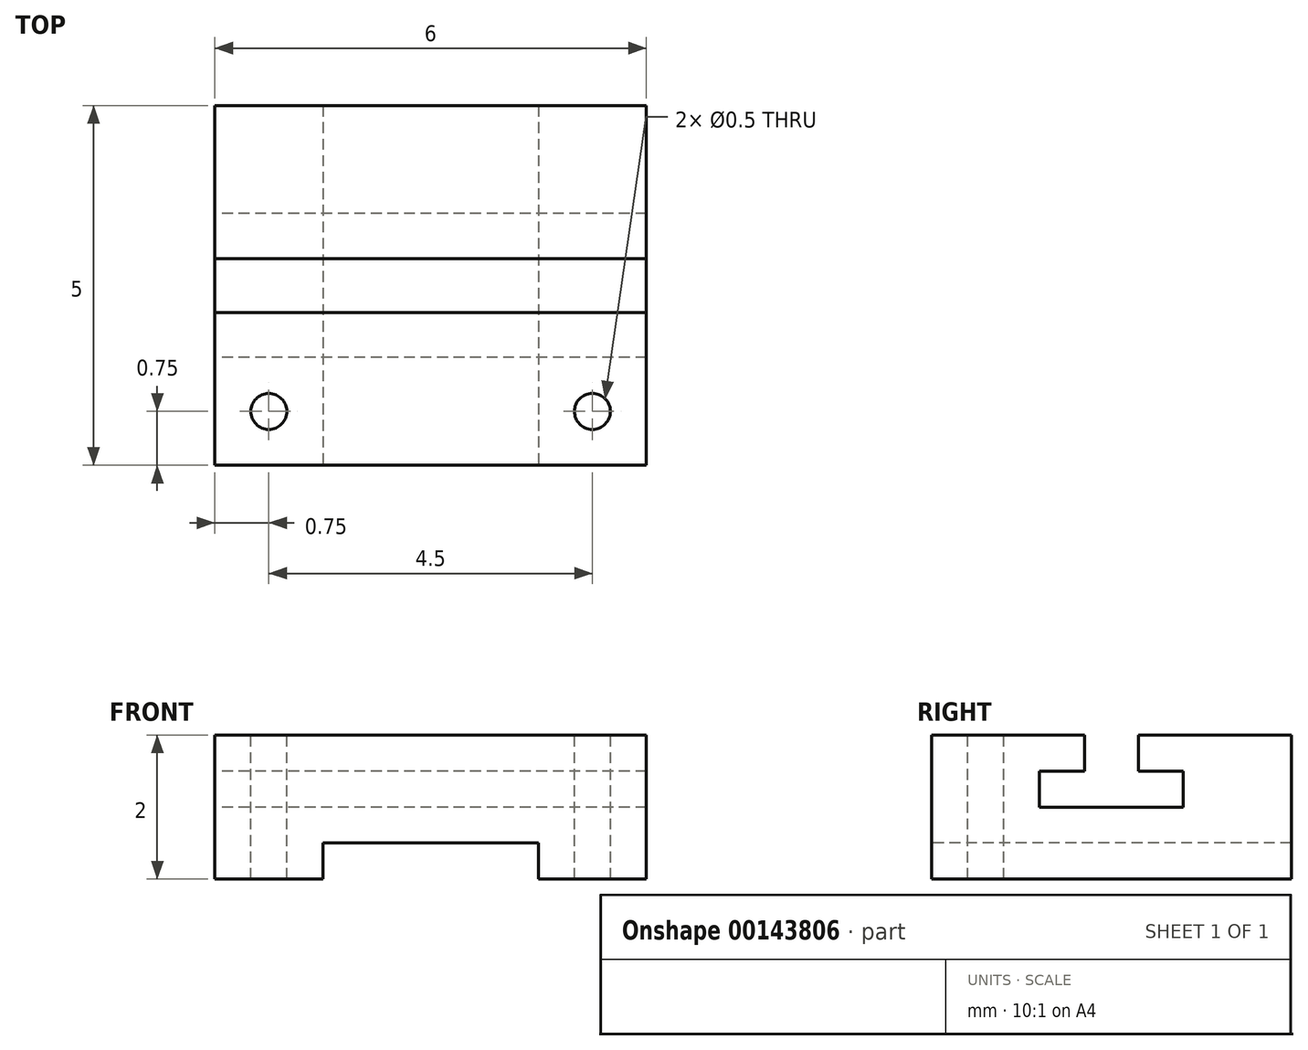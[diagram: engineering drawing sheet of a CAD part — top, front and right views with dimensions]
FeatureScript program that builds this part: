
annotation { "Feature Type Name" : "Feature", "Feature Type Description" : "" }
export const myFeature = defineFeature(function(context is Context, id is Id, definition is map)
    precondition{}
    {
        {
            var Q0;
            Q0=qCreatedBy(makeId("Right.planeOp"),FACE);
            var sketch = newSketch(context, id + "F0", { "sketchPlane" : qUnion([Q0])});
            skLineSegment(sketch, "E0", {"start": v(0, 0) * mm, "end": v(0, 2) * mm});
            skLineSegment(sketch, "E1", {"start": v(0, 2) * mm, "end": v(2.12, 2) * mm});
            skLineSegment(sketch, "E2", {"start": v(2.12, 2) * mm, "end": v(2.12, 1.5) * mm});
            skLineSegment(sketch, "E3", {"start": v(2.12, 1.5) * mm, "end": v(1.5, 1.5) * mm});
            skLineSegment(sketch, "E4", {"start": v(1.5, 1.5) * mm, "end": v(1.5, 1) * mm});
            skLineSegment(sketch, "E5", {"start": v(1.5, 1) * mm, "end": v(3.5, 1) * mm});
            skLineSegment(sketch, "E6", {"start": v(3.5, 1) * mm, "end": v(3.5, 1.5) * mm});
            skLineSegment(sketch, "E7", {"start": v(3.5, 1.5) * mm, "end": v(2.88, 1.5) * mm});
            skLineSegment(sketch, "E8", {"start": v(2.88, 1.5) * mm, "end": v(2.88, 2) * mm});
            skLineSegment(sketch, "E9", {"start": v(2.88, 2) * mm, "end": v(5, 2) * mm});
            skLineSegment(sketch, "E10", {"start": v(5, 2) * mm, "end": v(5, 0) * mm});
            skLineSegment(sketch, "E11", {"start": v(5, 0) * mm, "end": v(0, 0) * mm});
            skSolve(sketch);
        }
        {
            var Q0;
            Q0 = qSketchRegion(id + "F0", true);
            extrude(context, id + "F1", {"entities" : qUnion([Q0]), "depth" : 6 * mm});
        }
        {
            var Q0;
            Q0=makeQuery(id+"F1.opExtrude","SWEPT_FACE",FACE,{"disambiguationData":[OSD([sQuery(id+"F0.wireOp",EDGE,"E1")])]});
            var sketch = newSketch(context, id + "F2", { "sketchPlane" : qUnion([Q0])});
            skCircle(sketch, "E12", {"center": v(0.75, 0.75) * mm, "radius": 0.25 * mm});
            skCircle(sketch, "E13", {"center": v(5.25, 0.75) * mm, "radius": 0.25 * mm});
            skSolve(sketch);
        }
        {
            var Q0;
            Q0=makeQuery(id+"F2.imprint","IMPRINT",FACE,{"disambiguationData":[TD([[makeQuery(id+"F2.imprint","IMPRINT",EDGE,{"derivedFrom":sQuery(id+"F2.wireOp",EDGE,"E12")}),1.0]])]});
            var Q1;
            Q1=makeQuery(id+"F2.imprint","IMPRINT",FACE,{"disambiguationData":[TD([[makeQuery(id+"F2.imprint","IMPRINT",EDGE,{"derivedFrom":sQuery(id+"F2.wireOp",EDGE,"E13")}),1.0]])]});
            var Q2;
            Q2=sQuery(id+"F2.wireOp",EDGE,"E12");
            var Q3;
            Q3=sQuery(id+"F2.wireOp",EDGE,"E13");
            extrude(context, id + "F3", {"entities" : qUnion([Q0, Q1]), "operationType" : NewBodyOperationType.REMOVE, "surfaceEntities" : qUnion([Q2, Q3]), "oppositeDirection" : true, "depth" : 25 * mm});
        }
        {
            var Q0;
            Q0=makeQuery(id+"F1.opExtrude","SWEPT_FACE",FACE,{"disambiguationData":[OSD([sQuery(id+"F0.wireOp",EDGE,"E0")])]});
            var sketch = newSketch(context, id + "F4", { "sketchPlane" : qUnion([Q0])});
            skLineSegment(sketch, "E14", {"start": v(1.5, 0) * mm, "end": v(1.5, 0.5) * mm});
            skLineSegment(sketch, "E15", {"start": v(1.5, 0.5) * mm, "end": v(4.5, 0.5) * mm});
            skLineSegment(sketch, "E16", {"start": v(4.5, 0.5) * mm, "end": v(4.5, 0) * mm});
            skSolve(sketch);
        }
        {
            var Q0;
            {var subQ0=sQuery(id+"F4.wireOp",EDGE,"E14");Q0=makeQuery(id+"F4.imprint","IMPRINT",FACE,{"disambiguationData":[TD([[makeQuery(id+"F4.imprint","IMPRINT",EDGE,{"derivedFrom":subQ0}),-1.0]])]});}
            extrude(context, id + "F5", {"entities" : qUnion([Q0]), "operationType" : NewBodyOperationType.REMOVE, "oppositeDirection" : true, "depth" : 25 * mm});
        }
    });
